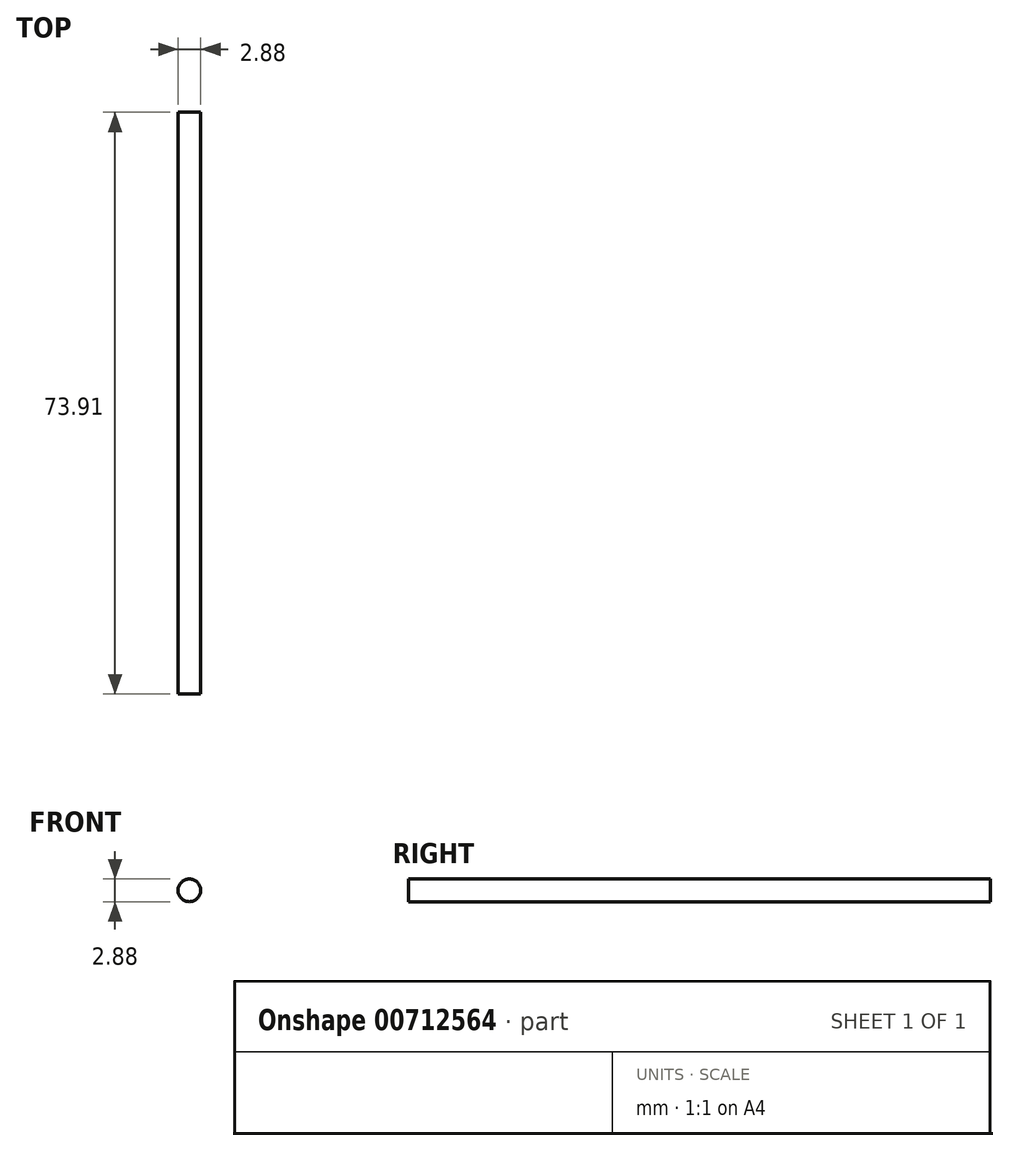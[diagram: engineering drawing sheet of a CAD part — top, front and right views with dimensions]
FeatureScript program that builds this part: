
annotation { "Feature Type Name" : "Feature", "Feature Type Description" : "" }
export const myFeature = defineFeature(function(context is Context, id is Id, definition is map)
    precondition{}
    {
        {
            var Q0;
            Q0=qCreatedBy(makeId("Front.planeOp"),FACE);
            var sketch = newSketch(context, id + "F0", { "sketchPlane" : qUnion([Q0])});
            skCircle(sketch, "E0", {"center": v(-32.1, 14.82) * mm, "radius": 1.44 * mm});
            skSolve(sketch);
        }
        {
            var Q0;
            Q0=sQuery(id+"F0.wireOp",EDGE,"E0");
            extrude(context, id + "F1", {"bodyType" : ToolBodyType.SURFACE, "surfaceEntities" : qUnion([Q0]), "depth" : 73.9 * mm, "offsetDistance" : 25.4 * mm});
        }
    });
